# Revit family: Clarus_Glide_R18
name_source: partatom
category: Furniture
revit_build: Autodesk Revit 2018 (Build: 20190510_1515(x64)
units: mm (PartAtom-declared; Revit-internal decimal feet)

## family parameters
Cut with Voids When Loaded = No
Host = Face
Room Calculation Point = No
Shared = No

## types (2) — shared parameters
Default Elevation = 0"
Depth = 3 3/4"
Description = For years, the fixed walls of modern office spaces have been steadily removed to create an open environment. Glide is the next step in the revolution, maximizing existing wall space to provide hundreds of consolidated square feet of glass writing surface and inspire personal communication and collaboration.
FMaxWidthH = 96"
FMaxWidthV = 48"
FMinWidthH = 36"
FMinWidthV = 36"
Fixed Panel Height = 45 1/2"
Hardware = Clarus Hardware
Manufacturer = Clarus
MaxHeightH = 50 1/2"
MaxHeightV = 98 1/2"
MaxWidthH = 96"
MaxWidthV = 48"
MinHeightH = 38 1/2"
MinHeightV = 38 1/2"
MinWidthH = 36"
MinWidthV = 36"
Model = Glide
Modeled By = Commense Studio
Product URL = https://www.clarus.com
Slider Height Control = 48"
Sliding Panel Height = 48"
URL = https://www.clarus.com

## per-type parameters (varying)
| type | Fixed Panel Width | Fixed Width Control | Horizontal Orientation | Slider Width Control | Sliding Panel Width | Vertical Orientation |
| Horizontal 96" Fixed x 48" Slider x 48" Height | 96" | 96" | Yes | 48" | 48" | No |
| Vertical 48" Fixed x 36" Slider x 48" Height | 48" | 48" | No | 36" | 36" | Yes |

## geometry (parser evidence)
native form markers: Sweep x4
no freeform markers — native parametric forms only
